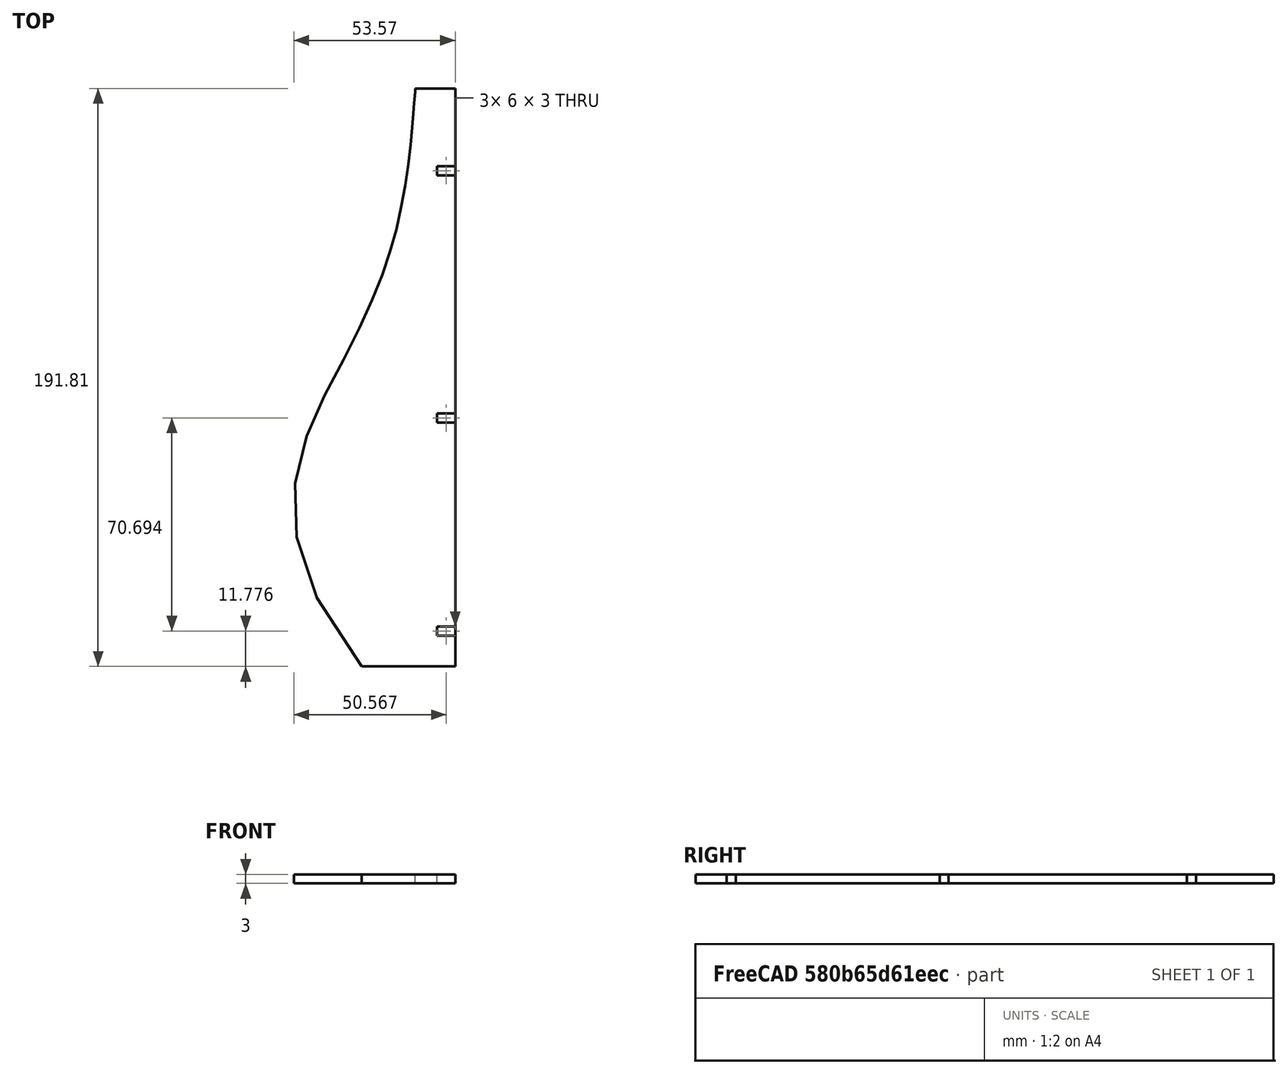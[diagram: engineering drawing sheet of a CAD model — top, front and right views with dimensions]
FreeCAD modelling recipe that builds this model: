
FCSTD DOCUMENT  (FreeCAD 1.0R38641 +678 (Git))
Label: VaseSide1
License: All rights reserved
LicenseURL: https://en.wikipedia.org/wiki/All_rights_reserved
objects: Sketcher::SketchObject×1, PartDesign::Pad×1, PartDesign::Body×1
note: 6 computed .brp shape members not serialized (recipe doc carries the construction recipe); baked Part::Feature solids carry a one-line shape summary decoded from their .brp

FEATURE [Sketcher::SketchObject] Sketch
  ArcFitTolerance = 1e-06
  AttachmentSupport = -> [XY_Plane]
  FullyConstrained = false
  MakeInternals = false
  MapMode = 5
  sketch-geometry (28):
    g0: LineSegment StartX=19.9974 StartY=93.2143 StartZ=0 EndX=19.9974 EndY=-98.6041 EndZ=0
    g1: LineSegment StartX=6.76327 StartY=93.2143 StartZ=0 EndX=19.9974 EndY=93.2143 EndZ=0
    g2: LineSegment StartX=19.9974 StartY=-88.3242 StartZ=0 EndX=19.9974 EndY=-85.3242 EndZ=0
    g3: LineSegment StartX=19.9974 StartY=-85.3242 StartZ=0 EndX=13.9974 EndY=-85.3242 EndZ=0
    g4: LineSegment StartX=13.9974 StartY=-85.3242 StartZ=0 EndX=13.9974 EndY=-88.3242 EndZ=0
    g5: LineSegment StartX=13.9974 StartY=-88.3242 StartZ=0 EndX=19.9974 EndY=-88.3242 EndZ=0
    g6: LineSegment StartX=19.9974 StartY=-98.6041 StartZ=0 EndX=-11.1146 EndY=-98.6041 EndZ=0
    g7-g13: Circle [constr] x7 (B-spline internal-alignment scaffolding for g14; pole/knot coordinates omitted)
    g14: BSplineCurve PolesCount=7 KnotsCount=5 Degree=3 IsPeriodic=0
    g15-g19: GeomPoint [constr] x5 (B-spline internal-alignment scaffolding for g14; pole/knot coordinates omitted)
    g20: LineSegment StartX=13.9974 StartY=-14.63 StartZ=0 EndX=13.9974 EndY=-17.63 EndZ=0
    g21: LineSegment StartX=13.9974 StartY=-17.63 StartZ=0 EndX=19.9974 EndY=-17.63 EndZ=0
    g22: LineSegment StartX=19.9974 StartY=-17.63 StartZ=0 EndX=19.9974 EndY=-14.63 EndZ=0
    g23: LineSegment StartX=19.9974 StartY=-14.63 StartZ=0 EndX=13.9974 EndY=-14.63 EndZ=0
    g24: LineSegment StartX=13.9974 StartY=67.4461 StartZ=0 EndX=13.9974 EndY=64.4461 EndZ=0
    g25: LineSegment StartX=13.9974 StartY=64.4461 StartZ=0 EndX=19.9974 EndY=64.4461 EndZ=0
    g26: LineSegment StartX=19.9974 StartY=64.4461 StartZ=0 EndX=19.9974 EndY=67.4461 EndZ=0
    g27: LineSegment StartX=19.9974 StartY=67.4461 StartZ=0 EndX=13.9974 EndY=67.4461 EndZ=0
  constraints (46):
    c: Vertical(g0)
    c: Coincident(g1,g0)
    c: Horizontal(g1)
    c: Coincident(g2,g3)
    c: Coincident(g3,g4)
    c: Coincident(g4,g5)
    c: Coincident(g5,g2)
    c: Vertical(g2)
    c: Vertical(g4)
    c: Horizontal(g3)
    c: Horizontal(g5)
    c: PointOnObject(g2,g0)
    c: Coincident(g6,g0)
    c: Horizontal(g6)
    c: Weight(g7) = 1
    c: Equal(g7, g8-g13) x6
    c: InternalAlignment(g7-g13 -> g14) x7
    c: InternalAlignment(g15-g19 -> g14) x5
    c: Coincident(g7,g6)
    c: Coincident(g11,g1)
    c: Coincident(g12,g1)
    c: Coincident(g13,g1)
    c: Coincident(g20,g21)
    c: Coincident(g21,g22)
    c: Coincident(g22,g23)
    c: Coincident(g23,g20)
    c: Vertical(g20)
    c: Vertical(g22)
    c: Horizontal(g21)
    c: Horizontal(g23)
    c: PointOnObject(g21,g0)
    c: Coincident(g24,g25)
    c: Coincident(g25,g26)
    c: Coincident(g26,g27)
    c: Coincident(g27,g24)
    c: Vertical(g24)
    c: Vertical(g26)
    c: Horizontal(g25)
    c: Horizontal(g27)
    c: PointOnObject(g25,g0)
    c: DistanceY(g24,g24) = 3
    c: DistanceY(g20,g20) = 3
    c: DistanceY(g4,g4) = 3
    c: DistanceX(g27,g27) = 6
    c: DistanceX(g23,g23) = 6
    c: DistanceX(g3,g3) = 6
FEATURE [PartDesign::Pad] Pad
  Direction = (0,0,1)
  Length = 3
  Length2 = 10
  Profile = -> Sketch
  ReferenceAxis = -> Sketch [N_Axis]
  Refine = true
  Suppressed = false
  Type = 0
FEATURE [PartDesign::Body] Body
  AllowCompound = false
  Group = -> [Sketch,Pad]
  Origin = -> Origin
  Tip = -> Pad
